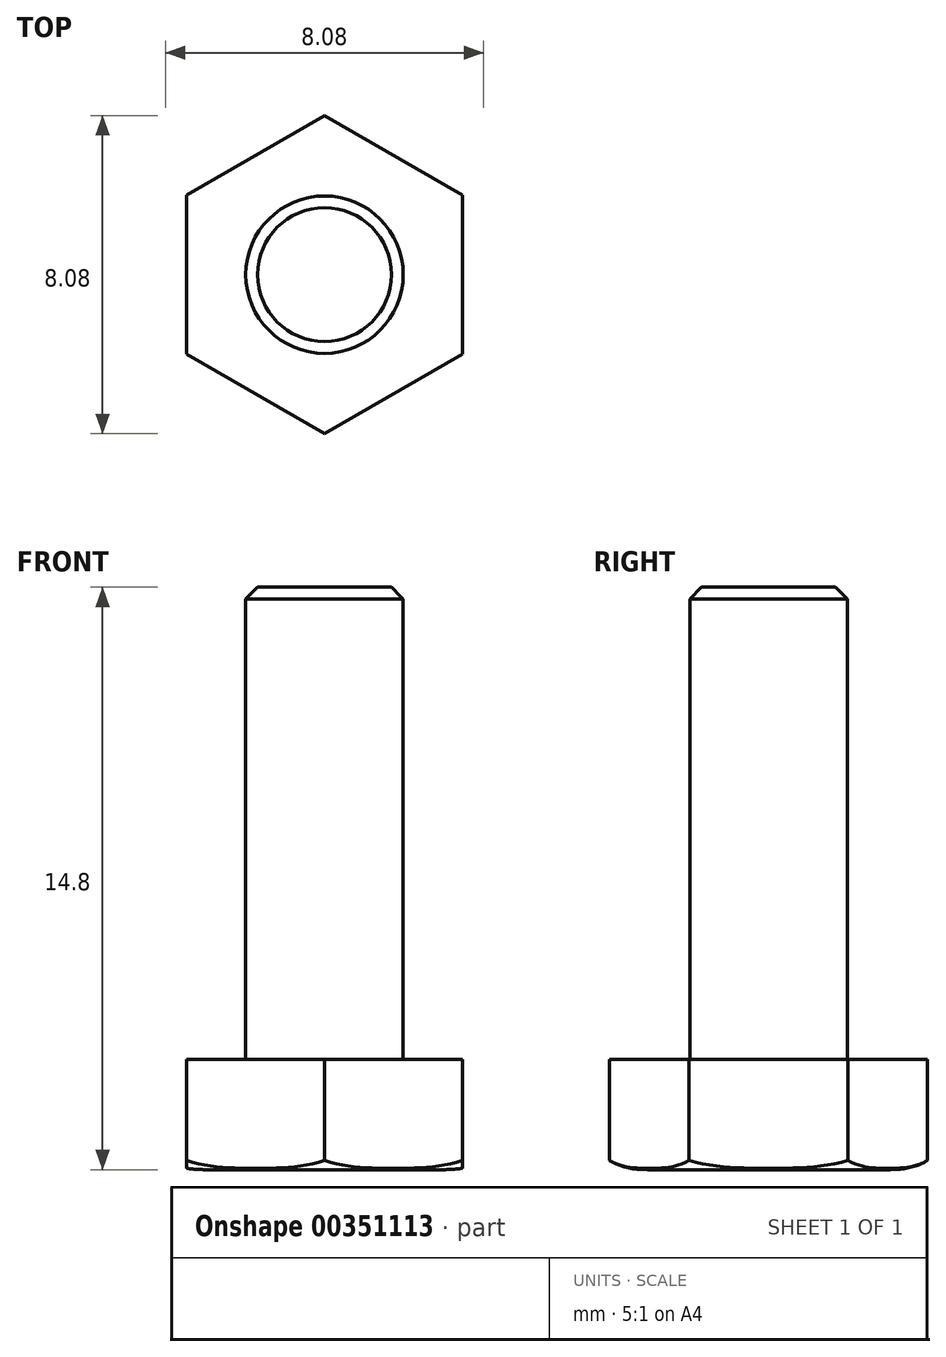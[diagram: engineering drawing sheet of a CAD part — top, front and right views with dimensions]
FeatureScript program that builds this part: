
annotation { "Feature Type Name" : "Feature", "Feature Type Description" : "" }
export const myFeature = defineFeature(function(context is Context, id is Id, definition is map)
    precondition{}
    {
        {
            var Q0;
            Q0=qCreatedBy(makeId("Top.planeOp"),FACE);
            var sketch = newSketch(context, id + "F0", { "sketchPlane" : qUnion([Q0])});
            skCircle(sketch, "E0", {"center": v(0, 0) * mm, "radius": 2 * mm});
            skLineSegment(sketch, "E1", {"start": v(0, 0) * mm, "end": v(0, 4.86) * mm, "construction": true});
            skCircle(sketch, "E2.cCircle", {"center": v(0, 0) * mm, "radius": 4.04 * mm, "construction": true});
            skLineSegment(sketch, "E2.0", {"start": v(0, 4.04) * mm, "end": v(3.5, 2.02) * mm});
            skLineSegment(sketch, "E2.1", {"start": v(3.5, 2.02) * mm, "end": v(3.5, -2.02) * mm});
            skLineSegment(sketch, "E2.2", {"start": v(3.5, -2.02) * mm, "end": v(0, -4.04) * mm});
            skLineSegment(sketch, "E2.3", {"start": v(0, -4.04) * mm, "end": v(-3.5, -2.02) * mm});
            skLineSegment(sketch, "E2.4", {"start": v(-3.5, -2.02) * mm, "end": v(-3.5, 2.02) * mm});
            skLineSegment(sketch, "E2.5", {"start": v(-3.5, 2.02) * mm, "end": v(0, 4.04) * mm});
            skSolve(sketch);
        }
        {
            var Q0;
            Q0=makeQuery(id+"F0.imprint","IMPRINT",FACE,{"disambiguationData":[TD([[makeQuery(id+"F0.imprint","IMPRINT",EDGE,{"derivedFrom":sQuery(id+"F0.wireOp",EDGE,"E0")}),1.0]])]});
            extrude(context, id + "F1", {"entities" : qUnion([Q0]), "depth" : 14.8 * mm});
        }
        {
            var Q0;
            Q0=makeQuery(id+"F0.imprint","IMPRINT",FACE,{"disambiguationData":[TD([[makeQuery(id+"F0.imprint","IMPRINT",EDGE,{"derivedFrom":sQuery(id+"F0.wireOp",EDGE,"E0")}),-1.0]])]});
            extrude(context, id + "F2", {"entities" : qUnion([Q0]), "operationType" : NewBodyOperationType.ADD, "depth" : 2.8 * mm});
        }
        {
            var Q0;
            Q0=qCreatedBy(makeId("Right.planeOp"),FACE);
            var sketch = newSketch(context, id + "F3", { "sketchPlane" : qUnion([Q0])});
            skFitSpline(sketch, "E3", {"points": [v(2.86, 0) * mm, v(4.04, 0.24) * mm], "startDerivative": vector(1.34, 0) * mm, "endDerivative": vector(1.17, 0.7) * mm});
            skLineSegment(sketch, "E4", {"start": v(2.86, 0) * mm, "end": v(4.04, 0) * mm});
            skLineSegment(sketch, "E5", {"start": v(4.04, 0) * mm, "end": v(4.04, 0.24) * mm});
            skSolve(sketch);
        }
        {
            var Q0;
            Q0=makeQuery(id+"F3.imprint","IMPRINT",FACE,{"disambiguationData":[TD([[makeQuery(id+"F3.imprint","IMPRINT",EDGE,{"derivedFrom":sQuery(id+"F3.wireOp",EDGE,"E3")}),-1.0]])]});
            var Q1;
            Q1=makeQuery(id+"F1.opExtrude","SWEPT_FACE",FACE,{"disambiguationData":[OSD([sQuery(id+"F0.wireOp",EDGE,"E0")])]});
            revolve(context, id + "F4", {"operationType" : NewBodyOperationType.REMOVE, "entities" : qUnion([Q0]), "axis" : qUnion([Q1]), "revolveType" : RevolveType.FULL, "oppositeDirection" : true});
        }
        {
            var Q0;
            Q0=makeQuery(id+"F1.opExtrude","CAP_EDGE",EDGE,{"disambiguationData":[OSD([sQuery(id+"F0.wireOp",EDGE,"E0")])],"isStart":false});
            chamfer(context, id + "F5", {"entities" : qUnion([Q0]), "width" : .3 * mm, "tangentPropagation" : true});
        }
    });
